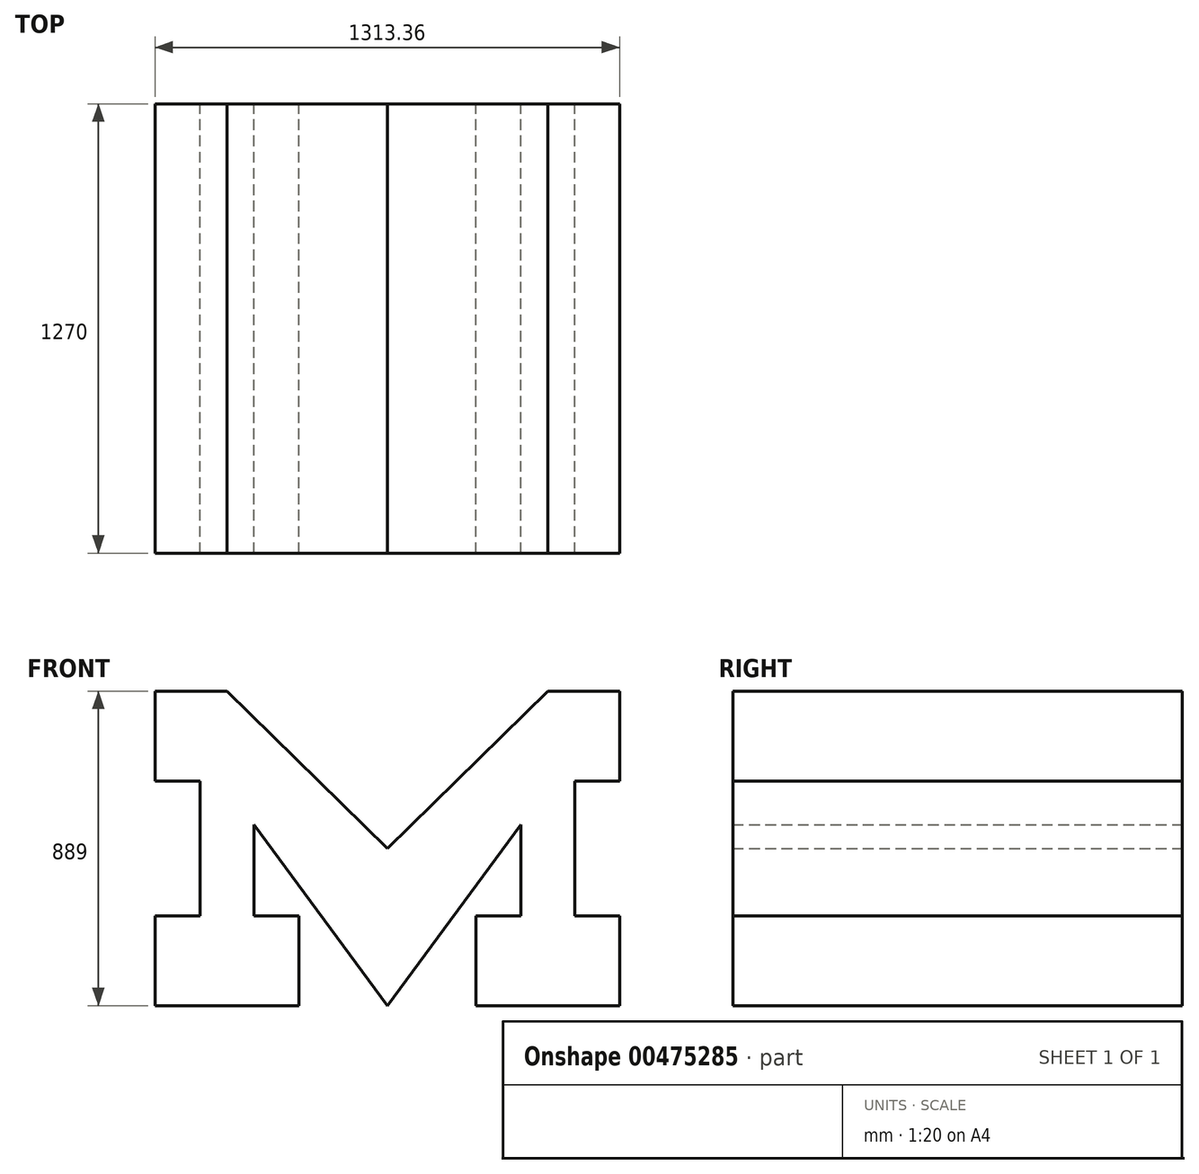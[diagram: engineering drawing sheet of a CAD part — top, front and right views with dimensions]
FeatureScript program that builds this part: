
annotation { "Feature Type Name" : "Feature", "Feature Type Description" : "" }
export const myFeature = defineFeature(function(context is Context, id is Id, definition is map)
    precondition{}
    {
        {
            var Q0;
            Q0=qCreatedBy(makeId("Front.planeOp"),FACE);
            var sketch = newSketch(context, id + "F0", { "sketchPlane" : qUnion([Q0])});
            skLineSegment(sketch, "E0", {"start": v(0, 0) * mm, "end": v(0, -254) * mm});
            skLineSegment(sketch, "E1", {"start": v(0, 0) * mm, "end": v(127, 0) * mm});
            skLineSegment(sketch, "E2", {"start": v(127, 0) * mm, "end": v(127, 381) * mm});
            skLineSegment(sketch, "E3", {"start": v(127, 381) * mm, "end": v(0, 381) * mm});
            skLineSegment(sketch, "E4", {"start": v(0, 381) * mm, "end": v(0, 635) * mm});
            skLineSegment(sketch, "E5", {"start": v(0, 635) * mm, "end": v(203.2, 635) * mm});
            skLineSegment(sketch, "E6", {"start": v(203.2, 635) * mm, "end": v(656.68, 190.5) * mm});
            skLineSegment(sketch, "E7", {"start": v(656.68, 190.5) * mm, "end": v(1110.16, 635) * mm});
            skLineSegment(sketch, "E8", {"start": v(1110.16, 635) * mm, "end": v(1313.36, 635) * mm});
            skLineSegment(sketch, "E9", {"start": v(1313.36, 635) * mm, "end": v(1313.36, 381) * mm});
            skLineSegment(sketch, "E10", {"start": v(1313.36, 381) * mm, "end": v(1186.36, 381) * mm});
            skLineSegment(sketch, "E11", {"start": v(1186.36, 381) * mm, "end": v(1186.36, 0) * mm});
            skLineSegment(sketch, "E12", {"start": v(1186.36, 0) * mm, "end": v(1313.36, 0) * mm});
            skLineSegment(sketch, "E13", {"start": v(1313.36, 0) * mm, "end": v(1313.36, -254) * mm});
            skLineSegment(sketch, "E14", {"start": v(1313.36, -254) * mm, "end": v(906.96, -254) * mm});
            skLineSegment(sketch, "E15", {"start": v(906.96, -254) * mm, "end": v(906.96, 0) * mm});
            skLineSegment(sketch, "E16", {"start": v(906.96, 0) * mm, "end": v(1033.96, 0) * mm});
            skLineSegment(sketch, "E17", {"start": v(0, -254) * mm, "end": v(406.4, -254) * mm});
            skLineSegment(sketch, "E18", {"start": v(406.4, -254) * mm, "end": v(406.4, 0) * mm});
            skLineSegment(sketch, "E19", {"start": v(406.4, 0) * mm, "end": v(279.4, 0) * mm});
            skLineSegment(sketch, "E20", {"start": v(279.4, 0) * mm, "end": v(279.4, 256.77) * mm});
            skLineSegment(sketch, "E21", {"start": v(279.4, 256.77) * mm, "end": v(656.68, -254) * mm});
            skLineSegment(sketch, "E22", {"start": v(656.68, -254) * mm, "end": v(1033.96, 256.77) * mm});
            skLineSegment(sketch, "E23", {"start": v(1033.96, 0) * mm, "end": v(1033.96, 256.77) * mm});
            skPoint(sketch, "E24.orphan", {"position": v(1705.97, -82.62) * mm});
            skSolve(sketch);
        }
        {
            var Q0;
            Q0=makeQuery(id+"F0.imprint","IMPRINT",FACE,{"disambiguationData":[TD([[makeQuery(id+"F0.imprint","IMPRINT",EDGE,{"derivedFrom":sQuery(id+"F0.wireOp",EDGE,"E0")}),1.0]])]});
            extrude(context, id + "F1", {"entities" : qUnion([Q0]), "depth" : 1270 * mm});
        }
        {
            var Q0;
            Q0=makeQuery(id+"F1.opExtrude","CAP_FACE",FACE,{"disambiguationData":[OSD([sQuery(id+"F0.wireOp",EDGE,"E0"),sQuery(id+"F0.wireOp",EDGE,"E1"),sQuery(id+"F0.wireOp",EDGE,"E2"),sQuery(id+"F0.wireOp",EDGE,"E3"),sQuery(id+"F0.wireOp",EDGE,"E4"),sQuery(id+"F0.wireOp",EDGE,"E5"),sQuery(id+"F0.wireOp",EDGE,"E6"),sQuery(id+"F0.wireOp",EDGE,"E7"),sQuery(id+"F0.wireOp",EDGE,"E8"),sQuery(id+"F0.wireOp",EDGE,"E9"),sQuery(id+"F0.wireOp",EDGE,"E10"),sQuery(id+"F0.wireOp",EDGE,"E11"),sQuery(id+"F0.wireOp",EDGE,"E12"),sQuery(id+"F0.wireOp",EDGE,"E13"),sQuery(id+"F0.wireOp",EDGE,"E14"),sQuery(id+"F0.wireOp",EDGE,"E15"),sQuery(id+"F0.wireOp",EDGE,"E16"),sQuery(id+"F0.wireOp",EDGE,"E17"),sQuery(id+"F0.wireOp",EDGE,"E18"),sQuery(id+"F0.wireOp",EDGE,"E19"),sQuery(id+"F0.wireOp",EDGE,"E20"),sQuery(id+"F0.wireOp",EDGE,"E21"),sQuery(id+"F0.wireOp",EDGE,"E22"),sQuery(id+"F0.wireOp",EDGE,"E23"),sQuery(id+"F0.wireOp",EDGE,"Ycggtqun-RqHU-E2Fw-Y1sm-pTJdw4BJe6Jy"),sQuery(id+"F0.wireOp",EDGE,"VWDA3aqO-UIMf-sc1t-O8xc-9r4w2ImlbvKs"),sQuery(id+"F0.wireOp",EDGE,"OmgMDpZF-kioa-Bf52-jSyy-pGYs9lKAcosx"),sQuery(id+"F0.wireOp",EDGE,"tW25DlYk-NjHI-qv15-xpUs-XIfaLt1uKQ1p"),sQuery(id+"F0.wireOp",EDGE,"xYvsOsNi-85YB-qdpP-rZNp-91wOdr0ip2OL"),sQuery(id+"F0.wireOp",EDGE,"FEHIJHZY-iBL7-kdCE-3utT-UHjxPACAErFX"),sQuery(id+"F0.wireOp",EDGE,"TxkYoBQH-2kOp-Keq0-FvYa-p1C1zGpfab65"),sQuery(id+"F0.wireOp",EDGE,"E6uRryqG-amo9-SpD8-eRnU-SkiqpyATr4sp"),sQuery(id+"F0.wireOp",EDGE,"6cY0sWJt-KYDD-AZsM-XU1X-NAewbp6VX7wl"),sQuery(id+"F0.wireOp",EDGE,"W1NF5q3V-bmqF-QHEj-PHrq-mUf3O4LDfjPr"),sQuery(id+"F0.wireOp",EDGE,"u1rdFMwK-hs08-9lsB-YBHy-rN7BjrniZlsi"),sQuery(id+"F0.wireOp",EDGE,"gMhjpy6Z-3B8p-vRTD-6MW3-Jpwr4mMAfb5Y"),sQuery(id+"F0.wireOp",EDGE,"y1hykI3G-auOh-XrAX-9B3k-iYST2KBckpKt"),sQuery(id+"F0.wireOp",EDGE,"one9VTzk-Xx7D-7QxG-iOQ4-78fDnyphVgjG"),sQuery(id+"F0.wireOp",EDGE,"f3e7634b-f378-468a-8b80-8a703135b415.trimOffspring"),sQuery(id+"F0.wireOp",EDGE,"71cd03aa-3fee-4247-b15c-6ee50bb2f561.trimOffspring"),sQuery(id+"F0.wireOp",EDGE,"1BYYPYSb-kLjF-80AD-t62F-MXZffHe8nmo4"),sQuery(id+"F0.wireOp",EDGE,"nbwKhFeU-y6AE-1Np1-48NV-i6cAhhx3wPub"),sQuery(id+"F0.wireOp",EDGE,"OJTFekAj-eDgf-gTUp-jhBh-ovC4k33bbO7G"),sQuery(id+"F0.wireOp",EDGE,"BiJaldLn-V6eN-w8Bl-PlWE-vpACy2zVtHDi"),sQuery(id+"F0.wireOp",EDGE,"nbstT7xV-FT98-HmZZ-TEtF-EeTJO0gOmy28"),sQuery(id+"F0.wireOp",EDGE,"rsMQdDwb-ueJ6-M1X3-kr8D-n3YNuH0Klxk9"),sQuery(id+"F0.wireOp",EDGE,"GRlNaebA-g64c-AMkB-KpcY-n7cV6gkGRlpf"),sQuery(id+"F0.wireOp",EDGE,"DXrTfXUj-baOd-Qkwp-kKs8-oUT0yVRDsint"),sQuery(id+"F0.wireOp",EDGE,"d6NYjkRM-gYBd-Walh-HvPQ-sGymGjAHPOlC")])],"isStart":true});
            extrude(context, id + "F2", {"entities" : qUnion([Q0]), "operationType" : NewBodyOperationType.ADD, "oppositeDirection" : true, "depth" : 127 * mm});
        }
        {
            var Q0;
            Q0 = qSketchRegion(id + "F0", true);
            extrude(context, id + "F3", {"entities" : qUnion([Q0]), "operationType" : NewBodyOperationType.ADD, "depth" : 25.4 * mm});
        }
    });
